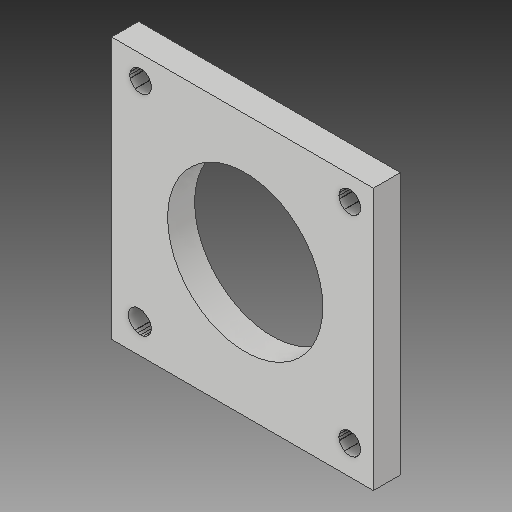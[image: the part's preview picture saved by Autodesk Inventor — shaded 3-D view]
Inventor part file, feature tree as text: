
AUTODESK INVENTOR PART (.ipt)
format: ipt  version: 2018 (Build 220112000, 112)  size: 179,200 bytes
history: native  units: mm
features: other x3, extrude x1, sketch x1, reference x1
ambient origin geometry x8: Origin, YZ Plane, XZ Plane, XY Plane, X Axis, Y Axis, Z Axis, Center Point
bodies: Solid1 (feature_tree)
feature tree (6):
  extrude  "Extrusion1"  Depth=4.0mm TaperAngle=0.0deg
  sketch  "Sketch1"  dims[d0=38.8mm d1=4.0mm d2=0.0mm d3=23.0mm]
  reference  "Reference1"
  other  "<userpath>\OneDrive\SL-Inventor\The Beast v1.2 PackandGo\Workspaces\Workspace\Assembly33.iam"
  other  "Assembly33.iam"
  other  "Z Motor Mount Right:1"
